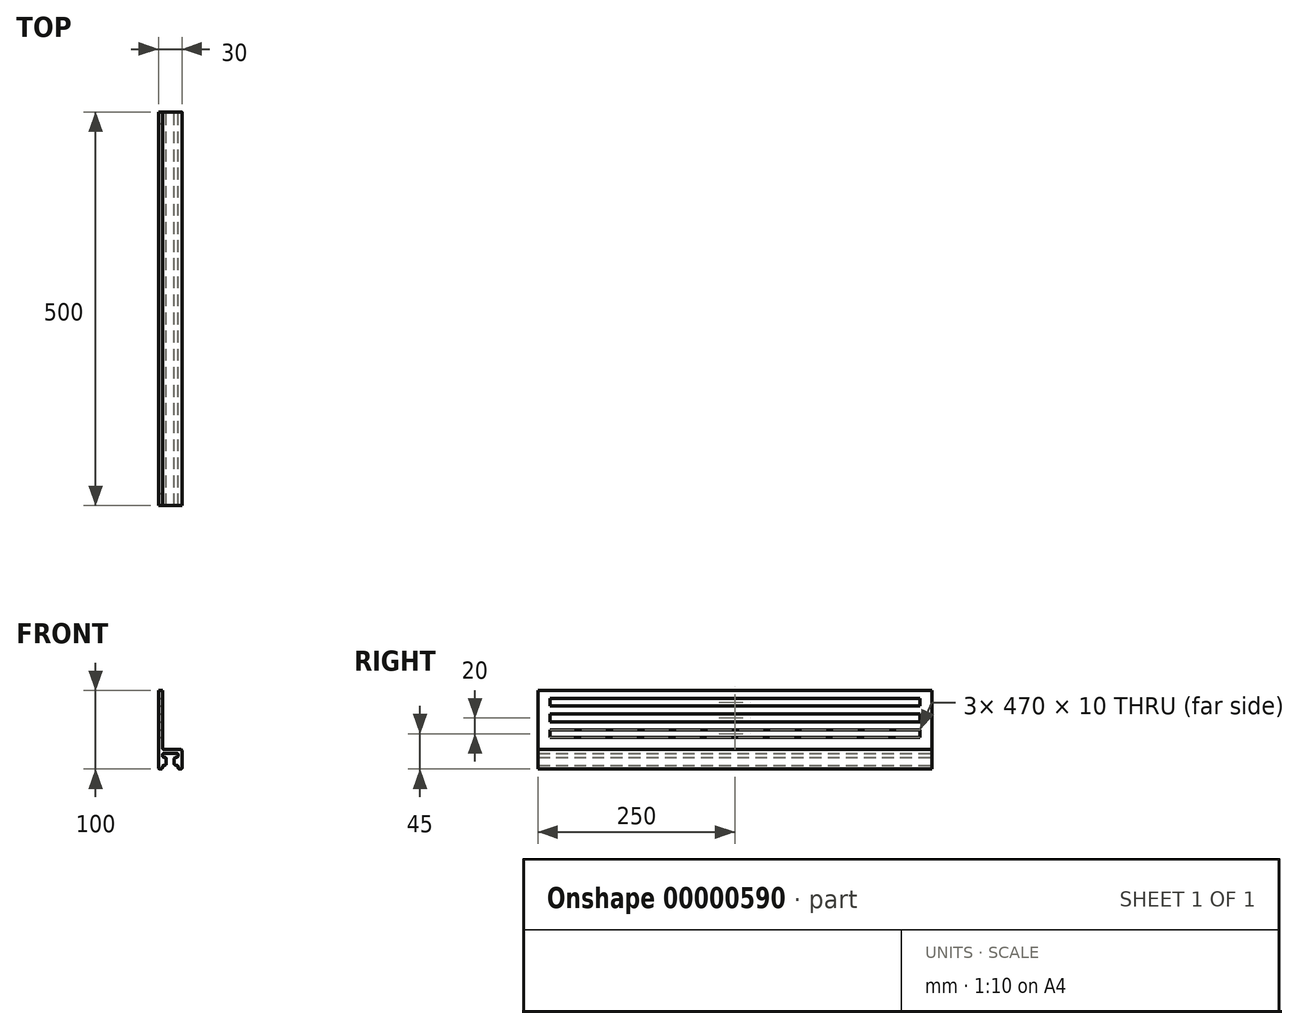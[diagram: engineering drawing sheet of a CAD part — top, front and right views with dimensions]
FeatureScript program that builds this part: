
annotation { "Feature Type Name" : "Feature", "Feature Type Description" : "" }
export const myFeature = defineFeature(function(context is Context, id is Id, definition is map)
    precondition{}
    {
        {
            var Q0;
            Q0 = qCreatedBy(makeId("Front.planeOp"), FACE);
            var sketch = newSketch(context, id + "F0", { "sketchPlane" : qUnion([Q0])});
            skLineSegment(sketch, "E0.rect.bottom", {"start": v(10, 10) * mm, "end": v(-10, 10) * mm});
            skLineSegment(sketch, "E0.rect.left", {"start": v(10, 10) * mm, "end": v(10, 5) * mm});
            skLineSegment(sketch, "E0.rect.right", {"start": v(-10, 10) * mm, "end": v(-10, 5) * mm});
            skPoint(sketch, "E0.rect.middle", {"position": v(0, 0) * mm});
            skLineSegment(sketch, "E1", {"start": v(10, -10) * mm, "end": v(15, -10) * mm});
            skLineSegment(sketch, "E2", {"start": v(15, -10) * mm, "end": v(15, 15) * mm});
            skLineSegment(sketch, "E3", {"start": v(15, 15) * mm, "end": v(-10, 15) * mm});
            skLineSegment(sketch, "E4", {"start": v(-10, 15) * mm, "end": v(-10, 90) * mm});
            skLineSegment(sketch, "E5", {"start": v(-10, 90) * mm, "end": v(-15, 90) * mm});
            skLineSegment(sketch, "E6", {"start": v(-15, 90) * mm, "end": v(-15, -10) * mm});
            skLineSegment(sketch, "E7", {"start": v(-15, -10) * mm, "end": v(-10, -10) * mm});
            skLineSegment(sketch, "E8", {"start": v(-10, 5) * mm, "end": v(-5, 5) * mm});
            skLineSegment(sketch, "E9", {"start": v(-5, 5) * mm, "end": v(-5, -5) * mm});
            skLineSegment(sketch, "E10", {"start": v(-5, -5) * mm, "end": v(-10, -5) * mm});
            skLineSegment(sketch, "E11", {"start": v(10, 5) * mm, "end": v(5, 5) * mm});
            skLineSegment(sketch, "E12", {"start": v(5, 5) * mm, "end": v(5, -5) * mm});
            skLineSegment(sketch, "E13", {"start": v(5, -5) * mm, "end": v(10, -5) * mm});
            skLineSegment(sketch, "E14.trimOffspring", {"start": v(-10, -5) * mm, "end": v(-10, -10) * mm});
            skLineSegment(sketch, "E15.trimOffspring", {"start": v(10, -5) * mm, "end": v(10, -10) * mm});
            skLineSegment(sketch, "E16", {"start": v(-10, 10) * mm, "end": v(10, -10) * mm, "construction": true});
            skSolve(sketch);
        }
        {
            var Q0;
            Q0=makeQuery(id+"F0.imprint","IMPRINT",FACE,{"disambiguationData":[TD([[makeQuery(id+"F0.imprint","IMPRINT",EDGE,{"derivedFrom":sQuery(id+"F0.wireOp",EDGE,"E0.rect.bottom")}),-1.0]])]});
            extrude(context, id + "F1", {"entities" : qUnion([Q0]), "endBound" : BoundingType.SYMMETRIC, "depth" : 500 * mm});
        }
        {
            var Q0;
            Q0=makeQuery(id+"F1.opExtrude","SWEPT_EDGE",EDGE,{"disambiguationData":[OSD([sQuery(id+"F0.wireOp",EDGE,"E3"),sQuery(id+"F0.wireOp",EDGE,"E4")])]});
            var Q1;
            Q1=makeQuery(id+"F1.opExtrude","SWEPT_EDGE",EDGE,{"disambiguationData":[OSD([sQuery(id+"F0.wireOp",EDGE,"E2"),sQuery(id+"F0.wireOp",EDGE,"E3")])]});
            var Q2;
            Q2=makeQuery(id+"F1.opExtrude","SWEPT_EDGE",EDGE,{"disambiguationData":[OSD([sQuery(id+"F0.wireOp",EDGE,"E1"),sQuery(id+"F0.wireOp",EDGE,"E2")])]});
            var Q3;
            Q3=makeQuery(id+"F1.opExtrude","SWEPT_EDGE",EDGE,{"disambiguationData":[OSD([sQuery(id+"F0.wireOp",EDGE,"E11"),sQuery(id+"F0.wireOp",EDGE,"E12")])]});
            var Q4;
            Q4=makeQuery(id+"F1.opExtrude","SWEPT_EDGE",EDGE,{"disambiguationData":[OSD([sQuery(id+"F0.wireOp",EDGE,"E0.rect.right"),sQuery(id+"F0.wireOp",EDGE,"E8")])]});
            var Q5;
            Q5=makeQuery(id+"F1.opExtrude","SWEPT_EDGE",EDGE,{"disambiguationData":[OSD([sQuery(id+"F0.wireOp",EDGE,"E8"),sQuery(id+"F0.wireOp",EDGE,"E9")])]});
            var Q6;
            Q6=makeQuery(id+"F1.opExtrude","SWEPT_EDGE",EDGE,{"disambiguationData":[OSD([sQuery(id+"F0.wireOp",EDGE,"E7"),sQuery(id+"F0.wireOp",EDGE,"E14.trimOffspring")])]});
            var Q7;
            Q7=makeQuery(id+"F1.opExtrude","SWEPT_EDGE",EDGE,{"disambiguationData":[OSD([sQuery(id+"F0.wireOp",EDGE,"E0.rect.bottom"),sQuery(id+"F0.wireOp",EDGE,"E0.rect.left")])]});
            var Q8;
            Q8=makeQuery(id+"F1.opExtrude","SWEPT_EDGE",EDGE,{"disambiguationData":[OSD([sQuery(id+"F0.wireOp",EDGE,"E12"),sQuery(id+"F0.wireOp",EDGE,"E13")])]});
            var Q9;
            Q9=makeQuery(id+"F1.opExtrude","SWEPT_EDGE",EDGE,{"disambiguationData":[OSD([sQuery(id+"F0.wireOp",EDGE,"E1"),sQuery(id+"F0.wireOp",EDGE,"E15.trimOffspring")])]});
            var Q10;
            Q10=makeQuery(id+"F1.opExtrude","SWEPT_EDGE",EDGE,{"disambiguationData":[OSD([sQuery(id+"F0.wireOp",EDGE,"E6"),sQuery(id+"F0.wireOp",EDGE,"E7")])]});
            var Q11;
            Q11=makeQuery(id+"F1.opExtrude","SWEPT_EDGE",EDGE,{"disambiguationData":[OSD([sQuery(id+"F0.wireOp",EDGE,"E10"),sQuery(id+"F0.wireOp",EDGE,"E14.trimOffspring")])]});
            var Q12;
            Q12=makeQuery(id+"F1.opExtrude","SWEPT_EDGE",EDGE,{"disambiguationData":[OSD([sQuery(id+"F0.wireOp",EDGE,"E9"),sQuery(id+"F0.wireOp",EDGE,"E10")])]});
            var Q13;
            Q13=makeQuery(id+"F1.opExtrude","SWEPT_EDGE",EDGE,{"disambiguationData":[OSD([sQuery(id+"F0.wireOp",EDGE,"E0.rect.bottom"),sQuery(id+"F0.wireOp",EDGE,"E0.rect.right")])]});
            var Q14;
            Q14=makeQuery(id+"F1.opExtrude","SWEPT_EDGE",EDGE,{"disambiguationData":[OSD([sQuery(id+"F0.wireOp",EDGE,"E0.rect.left"),sQuery(id+"F0.wireOp",EDGE,"E11")])]});
            var Q15;
            Q15=makeQuery(id+"F1.opExtrude","SWEPT_EDGE",EDGE,{"disambiguationData":[OSD([sQuery(id+"F0.wireOp",EDGE,"E13"),sQuery(id+"F0.wireOp",EDGE,"E15.trimOffspring")])]});
            fillet(context, id + "F2", {"entities" : qUnion([Q0, Q1, Q2, Q3, Q4, Q5, Q6, Q7, Q8, Q9, Q10, Q11, Q12, Q13, Q14, Q15]), "radius" : 2 * mm, "tangentPropagation" : true, "allowEdgeOverflow" : false});
        }
        {
            var Q0;
            Q0=makeQuery(id+"F1.opExtrude","SWEPT_FACE",FACE,{"disambiguationData":[OSD([sQuery(id+"F0.wireOp",EDGE,"E4")])]});
            var sketch = newSketch(context, id + "F3", { "sketchPlane" : qUnion([Q0])});
            skLineSegment(sketch, "E17.bottom", {"start": v(-235, 70) * mm, "end": v(235, 70) * mm});
            skLineSegment(sketch, "E17.top", {"start": v(-235, 80) * mm, "end": v(235, 80) * mm});
            skLineSegment(sketch, "E17.left", {"start": v(-235, 70) * mm, "end": v(-235, 80) * mm});
            skLineSegment(sketch, "E17.right", {"start": v(235, 70) * mm, "end": v(235, 80) * mm});
            skLineSegment(sketch, "E18.bottom", {"start": v(-235, 50) * mm, "end": v(235, 50) * mm});
            skLineSegment(sketch, "E18.top", {"start": v(-235, 60) * mm, "end": v(235, 60) * mm});
            skLineSegment(sketch, "E18.left", {"start": v(-235, 50) * mm, "end": v(-235, 60) * mm});
            skLineSegment(sketch, "E18.right", {"start": v(235, 50) * mm, "end": v(235, 60) * mm});
            skLineSegment(sketch, "E19.bottom", {"start": v(-235, 30) * mm, "end": v(235, 30) * mm});
            skLineSegment(sketch, "E19.top", {"start": v(-235, 40) * mm, "end": v(235, 40) * mm});
            skLineSegment(sketch, "E19.left", {"start": v(-235, 30) * mm, "end": v(-235, 40) * mm});
            skLineSegment(sketch, "E19.right", {"start": v(235, 30) * mm, "end": v(235, 40) * mm});
            skSolve(sketch);
        }
        {
            var Q0;
            {Q0=qUnion([makeQuery(id+"F3.imprint","IMPRINT",FACE,{"disambiguationData":[TD([[makeQuery(id+"F3.imprint","IMPRINT",EDGE,{"derivedFrom":sQuery(id+"F3.wireOp",EDGE,"E17.bottom")}),1.0]])]}),makeQuery(id+"F3.imprint","IMPRINT",FACE,{"disambiguationData":[TD([[makeQuery(id+"F3.imprint","IMPRINT",EDGE,{"derivedFrom":sQuery(id+"F3.wireOp",EDGE,"E18.bottom")}),1.0]])]}),makeQuery(id+"F3.imprint","IMPRINT",FACE,{"disambiguationData":[TD([[makeQuery(id+"F3.imprint","IMPRINT",EDGE,{"derivedFrom":sQuery(id+"F3.wireOp",EDGE,"E19.bottom")}),1.0]])]})]);}
            extrude(context, id + "F4", {"entities" : qUnion([Q0]), "operationType" : NewBodyOperationType.REMOVE, "endBound" : BoundingType.UP_TO_NEXT, "oppositeDirection" : true, "depth" : 25 * mm});
        }
    });
